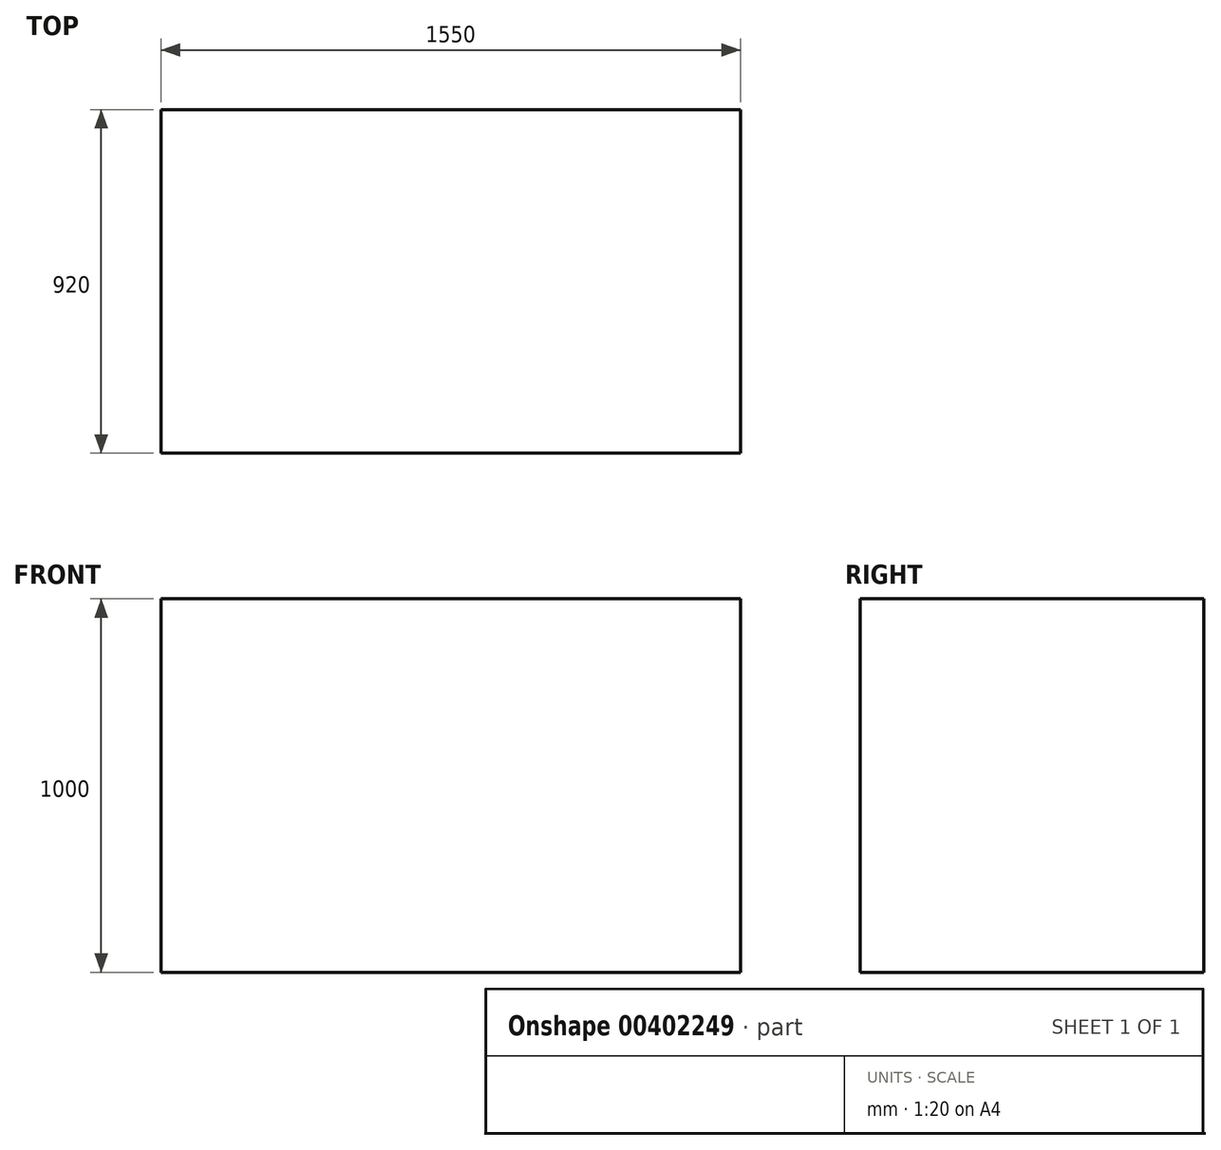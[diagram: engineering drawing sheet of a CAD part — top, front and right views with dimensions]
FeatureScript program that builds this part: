
annotation { "Feature Type Name" : "Feature", "Feature Type Description" : "" }
export const myFeature = defineFeature(function(context is Context, id is Id, definition is map)
    precondition{}
    {
        {
            var Q0;
            Q0=qCreatedBy(makeId("Top.planeOp"),FACE);
            var sketch = newSketch(context, id + "F0", { "sketchPlane" : qUnion([Q0])});
            skLineSegment(sketch, "E0.bottom", {"start": v(0, 0) * mm, "end": v(1550, 0) * mm});
            skLineSegment(sketch, "E0.top", {"start": v(0, 920) * mm, "end": v(1550, 920) * mm});
            skLineSegment(sketch, "E0.left", {"start": v(0, 0) * mm, "end": v(0, 920) * mm});
            skLineSegment(sketch, "E0.right", {"start": v(1550, 0) * mm, "end": v(1550, 920) * mm});
            skSolve(sketch);
        }
        {
            var Q0;
            Q0 = qSketchRegion(id + "F0", true);
            extrude(context, id + "F1", {"entities" : qUnion([Q0]), "depth" : 1000 * mm});
        }
    });
